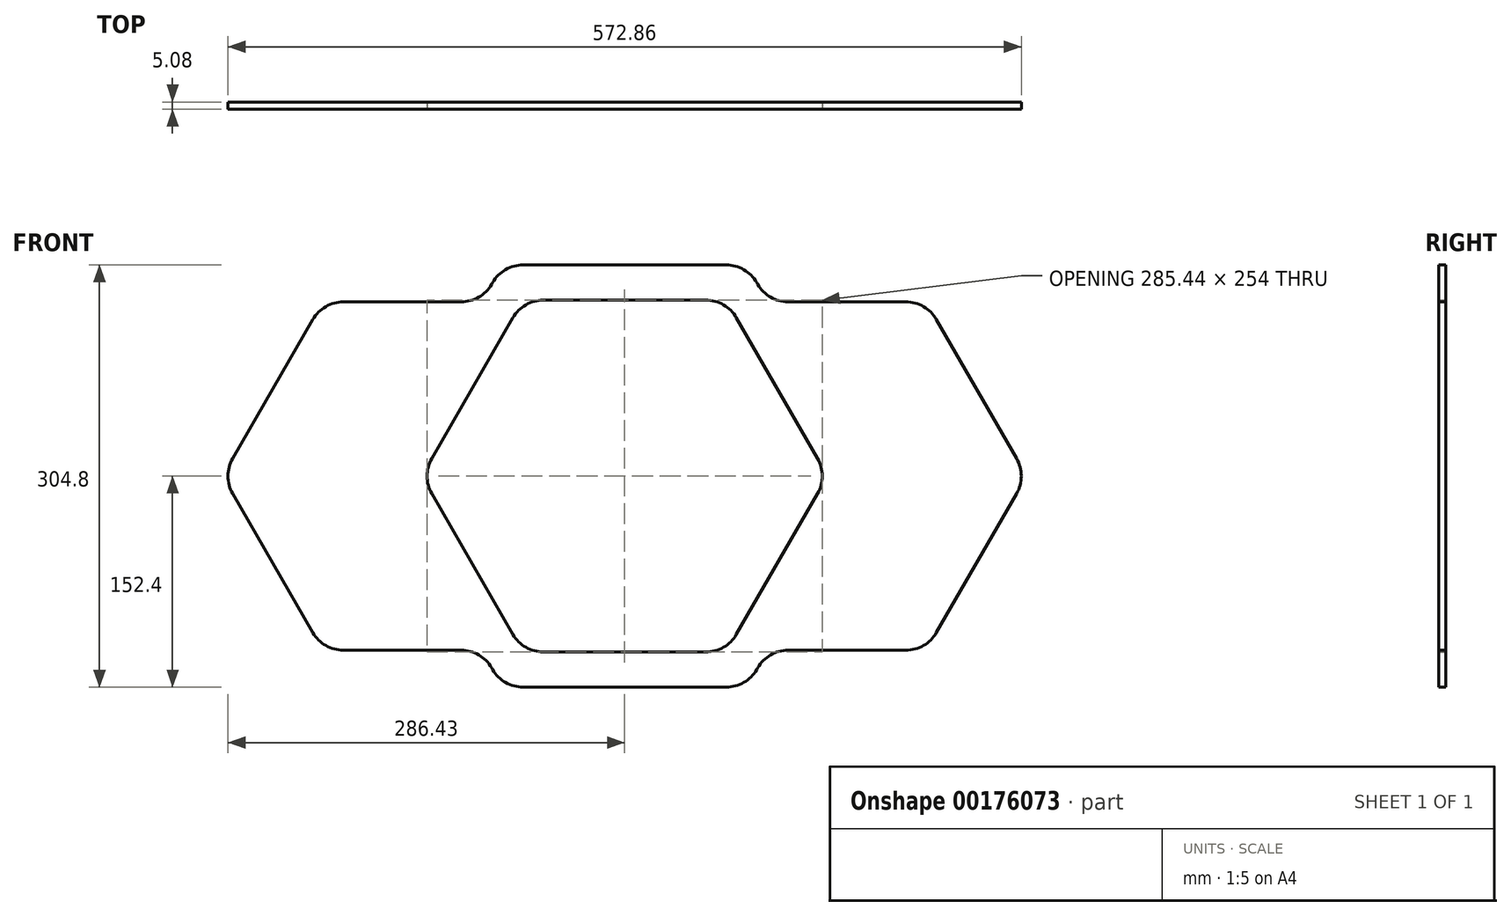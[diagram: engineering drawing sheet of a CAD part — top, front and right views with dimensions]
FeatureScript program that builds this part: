
annotation { "Feature Type Name" : "Feature", "Feature Type Description" : "" }
export const myFeature = defineFeature(function(context is Context, id is Id, definition is map)
    precondition{}
    {
        {
            var Q0;
            Q0=qCreatedBy(makeId("Front.planeOp"),FACE);
            var sketch = newSketch(context, id + "F0", { "sketchPlane" : qUnion([Q0])});
            skCircle(sketch, "E0.cCircle", {"center": v(0, 0) * mm, "radius": 125.73 * mm, "construction": true});
            skLineSegment(sketch, "E0.0", {"start": v(72.6, 125.73) * mm, "end": v(145.18, 0) * mm, "construction": true});
            skLineSegment(sketch, "E0.1", {"start": v(145.18, 0) * mm, "end": v(72.6, -125.73) * mm, "construction": true});
            skLineSegment(sketch, "E0.2", {"start": v(72.6, -125.73) * mm, "end": v(-72.6, -125.73) * mm});
            skLineSegment(sketch, "E0.3", {"start": v(-72.6, -125.73) * mm, "end": v(-145.18, 0) * mm});
            skLineSegment(sketch, "E0.4", {"start": v(-145.18, 0) * mm, "end": v(-72.6, 125.73) * mm});
            skLineSegment(sketch, "E0.5", {"start": v(-72.6, 125.73) * mm, "end": v(72.6, 125.73) * mm});
            skPoint(sketch, "E0.0.midPoint", {"position": v(108.89, 62.87) * mm});
            skCircle(sketch, "E1.cCircle", {"center": v(290.36, 0) * mm, "radius": 125.73 * mm, "construction": true});
            skLineSegment(sketch, "E1.0", {"start": v(362.95, 125.73) * mm, "end": v(435.54, 0) * mm});
            skLineSegment(sketch, "E1.1", {"start": v(435.54, 0) * mm, "end": v(362.95, -125.73) * mm});
            skLineSegment(sketch, "E1.2", {"start": v(362.95, -125.73) * mm, "end": v(217.77, -125.73) * mm});
            skLineSegment(sketch, "E1.3", {"start": v(217.77, -125.73) * mm, "end": v(145.18, 0) * mm, "construction": true});
            skLineSegment(sketch, "E1.4", {"start": v(145.18, 0) * mm, "end": v(217.77, 125.73) * mm, "construction": true});
            skLineSegment(sketch, "E1.5", {"start": v(217.77, 125.73) * mm, "end": v(362.95, 125.73) * mm});
            skPoint(sketch, "E1.0.midPoint", {"position": v(399.25, 62.87) * mm});
            skCircle(sketch, "E2.cCircle", {"center": v(145.18, 0) * mm, "radius": 127 * mm, "construction": true});
            skLineSegment(sketch, "E2.0", {"start": v(218.5, 127) * mm, "end": v(291.83, 0) * mm});
            skLineSegment(sketch, "E2.1", {"start": v(291.83, 0) * mm, "end": v(218.5, -127) * mm});
            skLineSegment(sketch, "E2.2", {"start": v(218.5, -127) * mm, "end": v(71.86, -127) * mm});
            skLineSegment(sketch, "E2.3", {"start": v(71.86, -127) * mm, "end": v(-1.47, 0) * mm});
            skLineSegment(sketch, "E2.4", {"start": v(-1.47, 0) * mm, "end": v(71.86, 127) * mm});
            skLineSegment(sketch, "E2.5", {"start": v(71.86, 127) * mm, "end": v(218.5, 127) * mm});
            skPoint(sketch, "E2.0.midPoint", {"position": v(255.17, 63.5) * mm});
            skCircle(sketch, "E3.cCircle", {"center": v(145.18, 0) * mm, "radius": 152.4 * mm, "construction": true});
            skLineSegment(sketch, "E3.0", {"start": v(57.2, 152.4) * mm, "end": v(233.17, 152.4) * mm});
            skLineSegment(sketch, "E3.1", {"start": v(233.17, 152.4) * mm, "end": v(321.16, 0) * mm});
            skLineSegment(sketch, "E3.2", {"start": v(321.16, 0) * mm, "end": v(233.17, -152.4) * mm});
            skLineSegment(sketch, "E3.3", {"start": v(233.17, -152.4) * mm, "end": v(57.2, -152.4) * mm});
            skLineSegment(sketch, "E3.4", {"start": v(57.2, -152.4) * mm, "end": v(-30.8, 0) * mm});
            skLineSegment(sketch, "E3.5", {"start": v(-30.8, 0) * mm, "end": v(57.2, 152.4) * mm});
            skPoint(sketch, "E3.0.midPoint", {"position": v(145.18, 152.4) * mm});
            skSolve(sketch);
        }
        {
            var Q0;
            {var subQ6=sQuery(id+"F0.wireOp",EDGE,"E0.3");Q0=makeQuery(id+"F0.imprint","IMPRINT",FACE,{"disambiguationData":[TD([[makeQuery(id+"F0.imprint","IMPRINT",EDGE,{"derivedFrom":subQ6}),-1.0]])]});}
            var Q1;
            {var subQ7=sQuery(id+"F0.wireOp",EDGE,"E0.2");var subQ9=sQuery(id+"F0.wireOp",EDGE,"E3.4");var subQ10=makeQuery(id+"F0.imprint","INTERSECT",VERTEX,{"derivedFrom":[subQ7,subQ9]});Q1=makeQuery(id+"F0.imprint","IMPRINT",FACE,{"disambiguationData":[TD([[makeQuery(id+"F0.imprint","IMPRINT",EDGE,{"disambiguationData":[TD([[subQ10,1.0]])],"derivedFrom":subQ7}),-1.0]])]});}
            var Q2;
            {var subQ0=sQuery(id+"F0.wireOp",EDGE,"E2.5");Q2=makeQuery(id+"F0.imprint","IMPRINT",FACE,{"disambiguationData":[TD([[makeQuery(id+"F0.imprint","IMPRINT",EDGE,{"derivedFrom":subQ0}),1.0]])]});}
            var Q3;
            {var subQ3=sQuery(id+"F0.wireOp",EDGE,"E1.2");var subQ5=sQuery(id+"F0.wireOp",EDGE,"E3.2");var subQ8=makeQuery(id+"F0.imprint","INTERSECT",VERTEX,{"derivedFrom":[subQ3,subQ5]});Q3=makeQuery(id+"F0.imprint","IMPRINT",FACE,{"disambiguationData":[TD([[makeQuery(id+"F0.imprint","IMPRINT",EDGE,{"disambiguationData":[TD([[subQ8,-1.0]])],"derivedFrom":subQ3}),-1.0]])]});}
            var Q4;
            {var subQ1=sQuery(id+"F0.wireOp",EDGE,"E1.0");Q4=makeQuery(id+"F0.imprint","IMPRINT",FACE,{"disambiguationData":[TD([[makeQuery(id+"F0.imprint","IMPRINT",EDGE,{"derivedFrom":subQ1}),-1.0]])]});}
            var Q5;
            {var subQ0=sQuery(id+"F0.wireOp",EDGE,"E2.2");Q5=makeQuery(id+"F0.imprint","IMPRINT",FACE,{"disambiguationData":[TD([[makeQuery(id+"F0.imprint","IMPRINT",EDGE,{"derivedFrom":subQ0}),1.0]])]});}
            extrude(context, id + "F1", {"entities" : qUnion([Q0, Q1, Q2, Q3, Q4, Q5]), "depth" : 5.08 * mm});
        }
        {
            var Q0;
            Q0=makeQuery(id+"F1.opExtrude","SWEPT_EDGE",EDGE,{"disambiguationData":[OSD([sQuery(id+"F0.wireOp",EDGE,"E0.5"),sQuery(id+"F0.wireOp",EDGE,"E3.5")])]});
            var Q1;
            Q1=makeQuery(id+"F1.opExtrude","SWEPT_EDGE",EDGE,{"disambiguationData":[OSD([sQuery(id+"F0.wireOp",EDGE,"E0.4"),sQuery(id+"F0.wireOp",EDGE,"E0.5")])]});
            var Q2;
            Q2=makeQuery(id+"F1.opExtrude","SWEPT_EDGE",EDGE,{"disambiguationData":[OSD([sQuery(id+"F0.wireOp",EDGE,"E0.3"),sQuery(id+"F0.wireOp",EDGE,"E0.4")])]});
            var Q3;
            Q3=makeQuery(id+"F1.opExtrude","SWEPT_EDGE",EDGE,{"disambiguationData":[OSD([sQuery(id+"F0.wireOp",EDGE,"E0.2"),sQuery(id+"F0.wireOp",EDGE,"E0.3")])]});
            var Q4;
            Q4=makeQuery(id+"F1.opExtrude","SWEPT_EDGE",EDGE,{"disambiguationData":[OSD([sQuery(id+"F0.wireOp",EDGE,"E0.2"),sQuery(id+"F0.wireOp",EDGE,"E3.4")])]});
            var Q5;
            Q5=makeQuery(id+"F1.opExtrude","SWEPT_EDGE",EDGE,{"disambiguationData":[OSD([sQuery(id+"F0.wireOp",EDGE,"E3.3"),sQuery(id+"F0.wireOp",EDGE,"E3.4")])]});
            var Q6;
            Q6=makeQuery(id+"F1.opExtrude","SWEPT_EDGE",EDGE,{"disambiguationData":[OSD([sQuery(id+"F0.wireOp",EDGE,"E3.2"),sQuery(id+"F0.wireOp",EDGE,"E3.3")])]});
            var Q7;
            Q7=makeQuery(id+"F1.opExtrude","SWEPT_EDGE",EDGE,{"disambiguationData":[OSD([sQuery(id+"F0.wireOp",EDGE,"E1.2"),sQuery(id+"F0.wireOp",EDGE,"E3.2")])]});
            var Q8;
            Q8=makeQuery(id+"F1.opExtrude","SWEPT_EDGE",EDGE,{"disambiguationData":[OSD([sQuery(id+"F0.wireOp",EDGE,"E1.1"),sQuery(id+"F0.wireOp",EDGE,"E1.2")])]});
            var Q9;
            Q9=makeQuery(id+"F1.opExtrude","SWEPT_EDGE",EDGE,{"disambiguationData":[OSD([sQuery(id+"F0.wireOp",EDGE,"E1.0"),sQuery(id+"F0.wireOp",EDGE,"E1.1")])]});
            var Q10;
            Q10=makeQuery(id+"F1.opExtrude","SWEPT_EDGE",EDGE,{"disambiguationData":[OSD([sQuery(id+"F0.wireOp",EDGE,"E1.0"),sQuery(id+"F0.wireOp",EDGE,"E1.5")])]});
            var Q11;
            Q11=makeQuery(id+"F1.opExtrude","SWEPT_EDGE",EDGE,{"disambiguationData":[OSD([sQuery(id+"F0.wireOp",EDGE,"E1.5"),sQuery(id+"F0.wireOp",EDGE,"E3.1")])]});
            var Q12;
            Q12=makeQuery(id+"F1.opExtrude","SWEPT_EDGE",EDGE,{"disambiguationData":[OSD([sQuery(id+"F0.wireOp",EDGE,"E3.0"),sQuery(id+"F0.wireOp",EDGE,"E3.1")])]});
            var Q13;
            Q13=makeQuery(id+"F1.opExtrude","SWEPT_EDGE",EDGE,{"disambiguationData":[OSD([sQuery(id+"F0.wireOp",EDGE,"E3.0"),sQuery(id+"F0.wireOp",EDGE,"E3.5")])]});
            var Q14;
            Q14=makeQuery(id+"F1.opExtrude","SWEPT_EDGE",EDGE,{"disambiguationData":[OSD([sQuery(id+"F0.wireOp",EDGE,"E2.4"),sQuery(id+"F0.wireOp",EDGE,"E2.5")])]});
            var Q15;
            Q15=makeQuery(id+"F1.opExtrude","SWEPT_EDGE",EDGE,{"disambiguationData":[OSD([sQuery(id+"F0.wireOp",EDGE,"E2.0"),sQuery(id+"F0.wireOp",EDGE,"E2.5")])]});
            var Q16;
            Q16=makeQuery(id+"F1.opExtrude","SWEPT_EDGE",EDGE,{"disambiguationData":[OSD([sQuery(id+"F0.wireOp",EDGE,"E2.0"),sQuery(id+"F0.wireOp",EDGE,"E2.1")])]});
            var Q17;
            Q17=makeQuery(id+"F1.opExtrude","SWEPT_EDGE",EDGE,{"disambiguationData":[OSD([sQuery(id+"F0.wireOp",EDGE,"E2.1"),sQuery(id+"F0.wireOp",EDGE,"E2.2")])]});
            var Q18;
            Q18=makeQuery(id+"F1.opExtrude","SWEPT_EDGE",EDGE,{"disambiguationData":[OSD([sQuery(id+"F0.wireOp",EDGE,"E2.2"),sQuery(id+"F0.wireOp",EDGE,"E2.3")])]});
            var Q19;
            Q19=makeQuery(id+"F1.opExtrude","SWEPT_EDGE",EDGE,{"disambiguationData":[OSD([sQuery(id+"F0.wireOp",EDGE,"E2.3"),sQuery(id+"F0.wireOp",EDGE,"E2.4")])]});
            fillet(context, id + "F2", {"entities" : qUnion([Q0, Q1, Q2, Q3, Q4, Q5, Q6, Q7, Q8, Q9, Q10, Q11, Q12, Q13, Q14, Q15, Q16, Q17, Q18, Q19]), "radius" : 25.4 * mm, "tangentPropagation" : true, "allowEdgeOverflow" : false});
        }
    });
